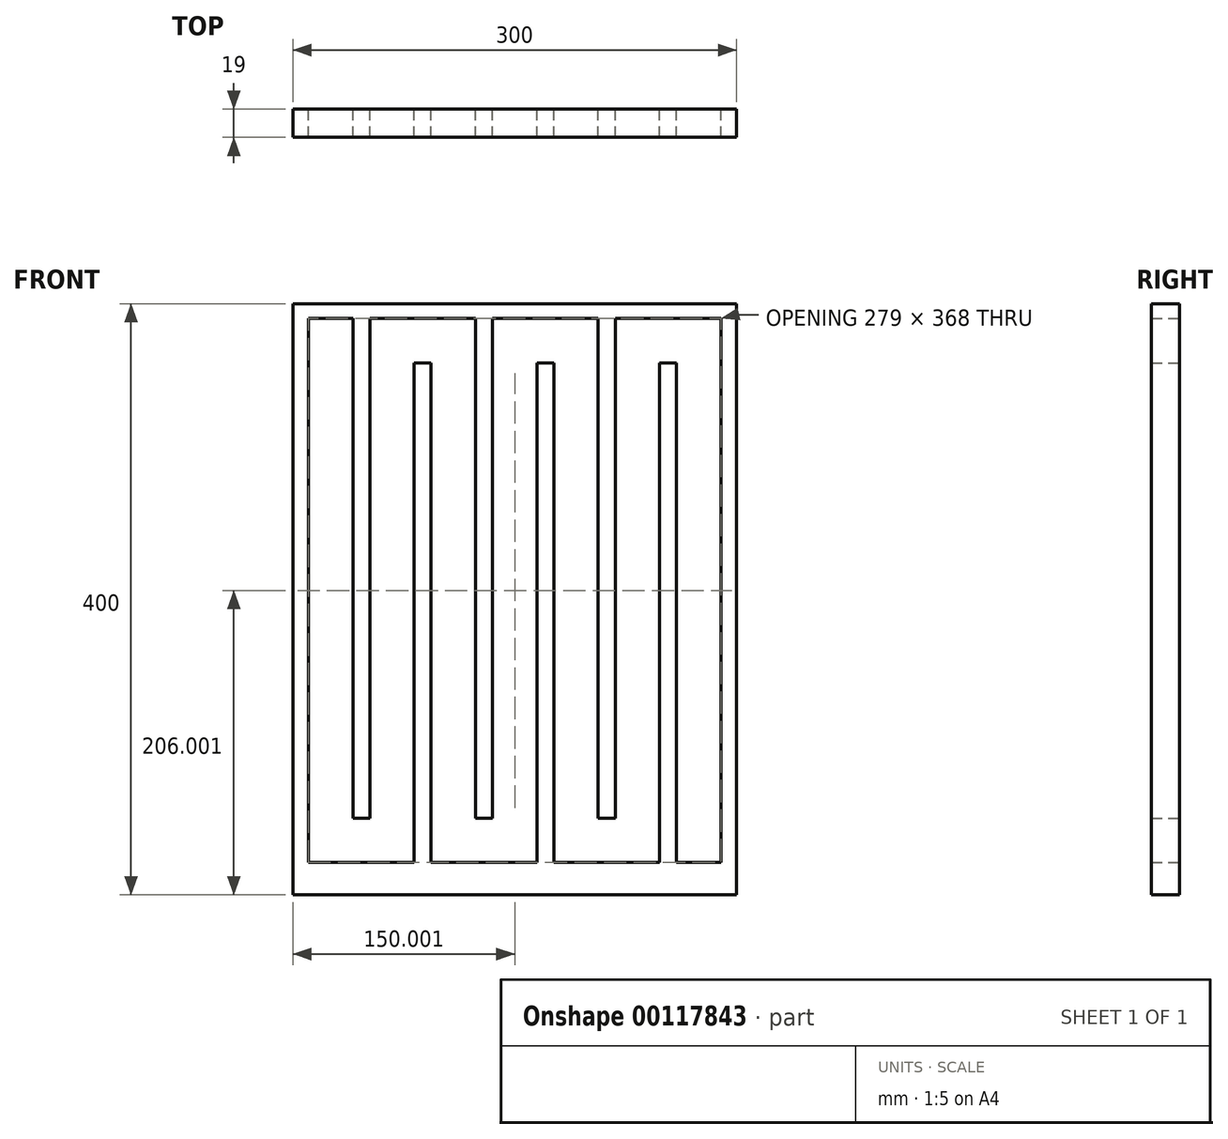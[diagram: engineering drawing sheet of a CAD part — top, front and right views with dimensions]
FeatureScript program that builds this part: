
annotation { "Feature Type Name" : "Feature", "Feature Type Description" : "" }
export const myFeature = defineFeature(function(context is Context, id is Id, definition is map)
    precondition{}
    {
        {
            var Q0;
            Q0=qCreatedBy(makeId("Front.planeOp"),FACE);
            var sketch = newSketch(context, id + "F0", { "sketchPlane" : qUnion([Q0])});
            skLineSegment(sketch, "E0.bottom", {"start": v(-318.07, 196.47) * mm, "end": v(-18.07, 196.47) * mm});
            skLineSegment(sketch, "E0.top", {"start": v(-318.07, -203.53) * mm, "end": v(-18.07, -203.53) * mm});
            skLineSegment(sketch, "E0.left", {"start": v(-318.07, 196.47) * mm, "end": v(-318.07, -203.53) * mm});
            skLineSegment(sketch, "E0.right", {"start": v(-18.07, 196.47) * mm, "end": v(-18.07, -203.53) * mm});
            skSolve(sketch);
        }
        {
            var Q0;
            Q0=makeQuery(id+"F0.imprint","IMPRINT",FACE,{"disambiguationData":[TD([[makeQuery(id+"F0.imprint","IMPRINT",EDGE,{"derivedFrom":sQuery(id+"F0.wireOp",EDGE,"E0.bottom")}),-1.0]])]});
            extrude(context, id + "F1", {"entities" : qUnion([Q0]), "depth" : 19 * mm});
        }
        {
            var Q0;
            Q0=makeQuery(id+"F1.opExtrude","CAP_FACE",FACE,{"disambiguationData":[OSD([sQuery(id+"F0.wireOp",EDGE,"E0.bottom"),sQuery(id+"F0.wireOp",EDGE,"E0.top"),sQuery(id+"F0.wireOp",EDGE,"E0.left"),sQuery(id+"F0.wireOp",EDGE,"E0.right")])],"isStart":true});
            var sketch = newSketch(context, id + "F2", { "sketchPlane" : qUnion([Q0])});
            skLineSegment(sketch, "E1", {"start": v(28.57, -181.53) * mm, "end": v(58.57, -181.53) * mm});
            skLineSegment(sketch, "E2", {"start": v(58.57, -181.53) * mm, "end": v(58.57, 156.47) * mm});
            skLineSegment(sketch, "E3", {"start": v(58.57, 156.47) * mm, "end": v(70.07, 156.47) * mm});
            skLineSegment(sketch, "E4", {"start": v(70.07, 156.47) * mm, "end": v(70.07, -181.53) * mm});
            skLineSegment(sketch, "E5", {"start": v(70.07, -181.53) * mm, "end": v(141.57, -181.53) * mm});
            skLineSegment(sketch, "E6", {"start": v(141.57, -181.53) * mm, "end": v(141.57, 156.47) * mm});
            skLineSegment(sketch, "E7", {"start": v(141.57, 156.47) * mm, "end": v(153.07, 156.47) * mm});
            skLineSegment(sketch, "E8", {"start": v(153.07, 156.47) * mm, "end": v(153.07, -181.53) * mm});
            skLineSegment(sketch, "E9", {"start": v(153.07, -181.53) * mm, "end": v(224.57, -181.53) * mm});
            skLineSegment(sketch, "E10", {"start": v(224.57, -181.53) * mm, "end": v(224.57, 156.47) * mm});
            skLineSegment(sketch, "E11", {"start": v(224.57, 156.47) * mm, "end": v(236.07, 156.47) * mm});
            skLineSegment(sketch, "E12", {"start": v(236.07, 156.47) * mm, "end": v(236.07, -181.53) * mm});
            skLineSegment(sketch, "E13", {"start": v(236.07, -181.53) * mm, "end": v(307.57, -181.53) * mm});
            skLineSegment(sketch, "E14", {"start": v(307.57, -181.53) * mm, "end": v(307.57, 186.47) * mm});
            skLineSegment(sketch, "E15", {"start": v(307.57, 186.47) * mm, "end": v(277.57, 186.47) * mm});
            skLineSegment(sketch, "E16", {"start": v(277.57, 186.47) * mm, "end": v(277.57, -151.53) * mm});
            skLineSegment(sketch, "E17", {"start": v(277.57, -151.53) * mm, "end": v(266.07, -151.53) * mm});
            skLineSegment(sketch, "E18", {"start": v(266.07, -151.53) * mm, "end": v(266.07, 186.47) * mm});
            skLineSegment(sketch, "E19", {"start": v(266.07, 186.47) * mm, "end": v(194.57, 186.47) * mm});
            skLineSegment(sketch, "E20", {"start": v(194.57, 186.47) * mm, "end": v(194.57, -151.53) * mm});
            skLineSegment(sketch, "E21", {"start": v(194.57, -151.53) * mm, "end": v(183.07, -151.53) * mm});
            skLineSegment(sketch, "E22", {"start": v(183.07, -151.53) * mm, "end": v(183.07, 186.47) * mm});
            skLineSegment(sketch, "E23", {"start": v(183.07, 186.47) * mm, "end": v(111.57, 186.47) * mm});
            skLineSegment(sketch, "E24", {"start": v(111.57, 186.47) * mm, "end": v(111.57, -151.53) * mm});
            skLineSegment(sketch, "E25", {"start": v(111.57, -151.53) * mm, "end": v(100.07, -151.53) * mm});
            skLineSegment(sketch, "E26", {"start": v(100.07, -151.53) * mm, "end": v(100.07, 186.47) * mm});
            skLineSegment(sketch, "E27", {"start": v(100.07, 186.47) * mm, "end": v(28.57, 186.47) * mm});
            skLineSegment(sketch, "E28", {"start": v(28.57, 186.47) * mm, "end": v(28.57, -181.53) * mm});
            skSolve(sketch);
        }
        {
            var Q0;
            Q0 = qSketchRegion(id + "F2", true);
            extrude(context, id + "F3", {"entities" : qUnion([Q0]), "operationType" : NewBodyOperationType.REMOVE, "oppositeDirection" : true, "depth" : 19 * mm});
        }
    });
